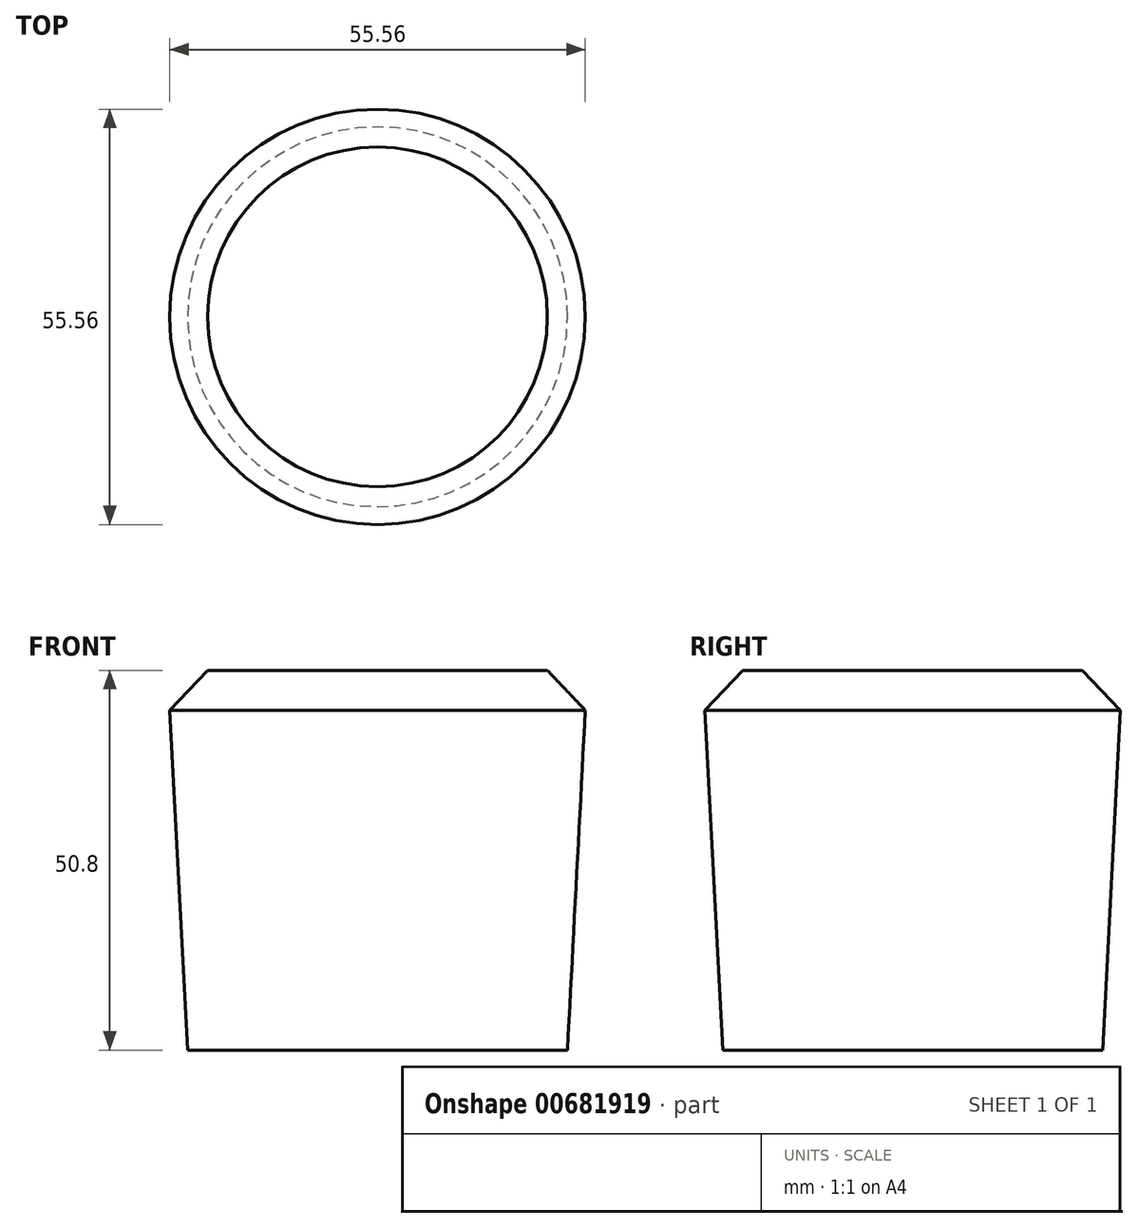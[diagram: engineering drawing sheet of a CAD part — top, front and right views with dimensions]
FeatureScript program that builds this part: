
annotation { "Feature Type Name" : "Feature", "Feature Type Description" : "" }
export const myFeature = defineFeature(function(context is Context, id is Id, definition is map)
    precondition{}
    {
        {
            var Q0;
            Q0=qCreatedBy(makeId("Top.planeOp"),FACE);
            var sketch = newSketch(context, id + "F0", { "sketchPlane" : qUnion([Q0])});
            skCircle(sketch, "E0", {"center": v(0, 0) * mm, "radius": 25.4 * mm});
            skSolve(sketch);
        }
        {
            var Q0;
            Q0 = qSketchRegion(id + "F0", true);
            extrude(context, id + "F1", {"entities" : qUnion([Q0]), "depth" : 50.8 * mm, "offsetDistance" : 25.4 * mm, "hasDraft" : true, "draftAngle" : 3 * degree});
        }
        {
            var Q0;
            Q0=makeQuery(id+"F1.opExtrude","CAP_FACE",FACE,{"disambiguationData":[OSD([sQuery(id+"F0.wireOp",EDGE,"E0")])],"isStart":false});
            chamfer(context, id + "F2", {"entities" : qUnion([Q0]), "width" : 5.08 * mm, "tangentPropagation" : true});
        }
    });
